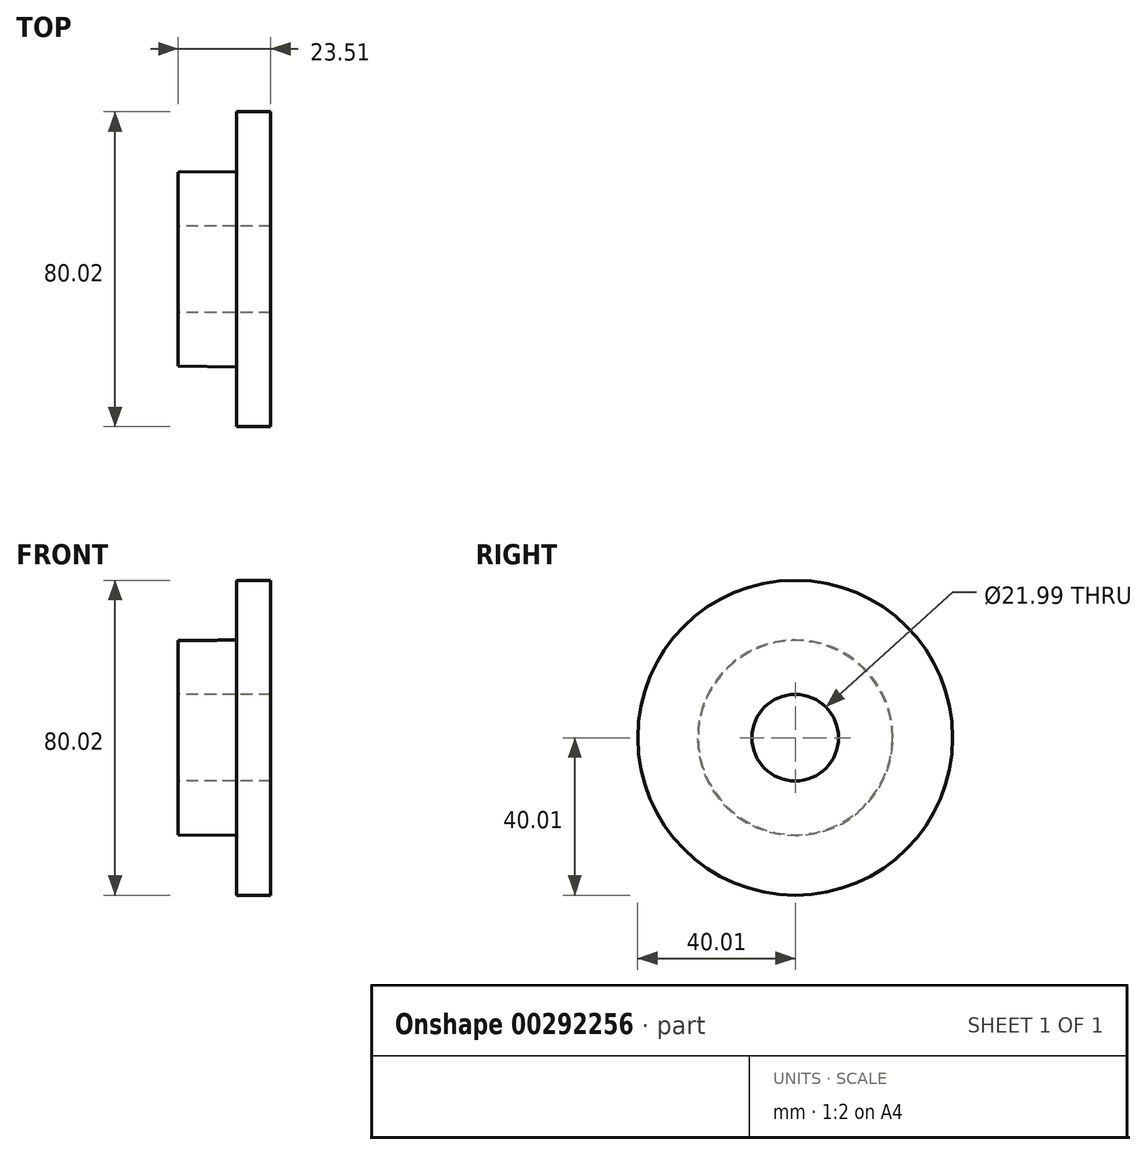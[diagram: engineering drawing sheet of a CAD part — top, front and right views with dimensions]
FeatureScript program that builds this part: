
annotation { "Feature Type Name" : "Feature", "Feature Type Description" : "" }
export const myFeature = defineFeature(function(context is Context, id is Id, definition is map)
    precondition{}
    {
        {
            var Q0;
            Q0=qCreatedBy(makeId("Front.planeOp"),FACE);
            var sketch = newSketch(context, id + "F0", { "sketchPlane" : qUnion([Q0])});
            skLineSegment(sketch, "E0", {"start": v(-42.1, 24.65) * mm, "end": v(-42.1, 11) * mm});
            skLineSegment(sketch, "E1", {"start": v(-42.1, 11) * mm, "end": v(-18.58, 11) * mm});
            skLineSegment(sketch, "E2", {"start": v(-18.58, 11) * mm, "end": v(-18.58, 40) * mm});
            skLineSegment(sketch, "E3", {"start": v(-18.58, 40) * mm, "end": v(-27.3, 40) * mm});
            skLineSegment(sketch, "E4", {"start": v(-27.3, 40) * mm, "end": v(-27.3, 24.84) * mm});
            skLineSegment(sketch, "E5", {"start": v(-27.3, 24.84) * mm, "end": v(-42.1, 24.65) * mm});
            skLineSegment(sketch, "E6", {"start": v(-47.97, 0) * mm, "end": v(0, 0) * mm, "construction": true});
            skSolve(sketch);
        }
        {
            var Q0;
            Q0 = qSketchRegion(id + "F0", true);
            var Q1;
            Q1=sQuery(id+"F0.wireOp",EDGE,"E6");
            revolve(context, id + "F1", {"entities" : qUnion([Q0]), "axis" : qUnion([Q1]), "revolveType" : RevolveType.FULL});
        }
    });
